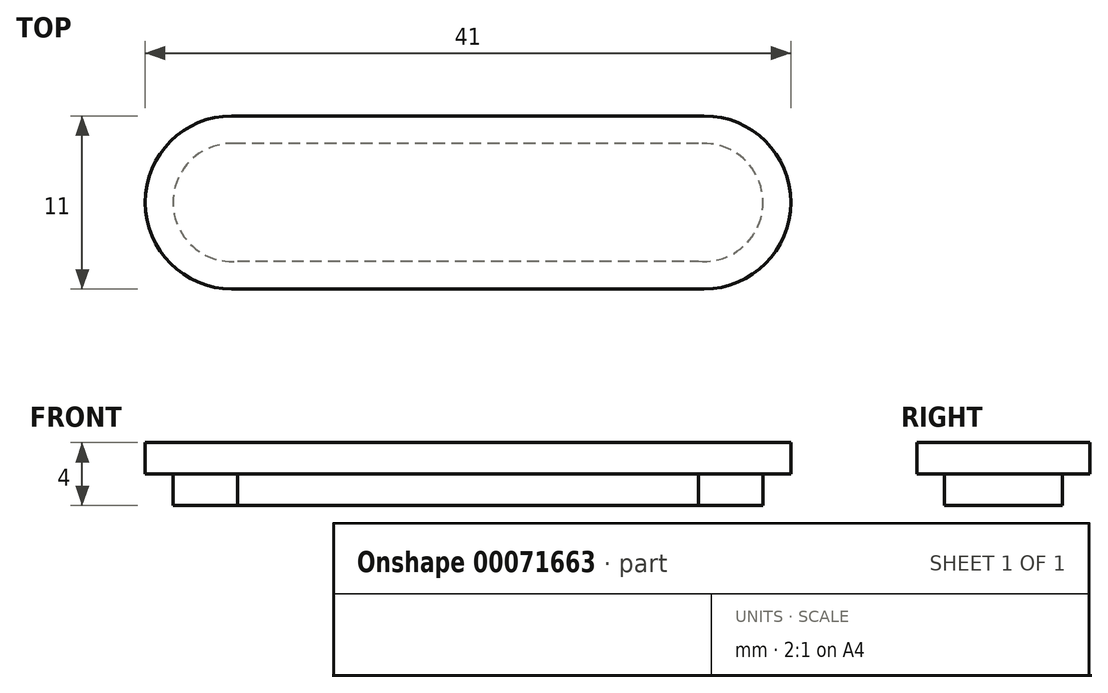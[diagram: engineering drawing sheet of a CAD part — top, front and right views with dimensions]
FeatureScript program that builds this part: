
annotation { "Feature Type Name" : "Feature", "Feature Type Description" : "" }
export const myFeature = defineFeature(function(context is Context, id is Id, definition is map)
    precondition{}
    {
        {
            var Q0;
            Q0=qCreatedBy(makeId("Top.planeOp"),FACE);
            var sketch = newSketch(context, id + "F0", { "sketchPlane" : qUnion([Q0])});
            skLineSegment(sketch, "E0.7", {"start": v(14.14, 5.47) * mm, "end": v(-15.86, 5.47) * mm});
            skLineSegment(sketch, "E0.6", {"start": v(14.14, 3.97) * mm, "end": v(-15.86, 3.97) * mm, "construction": true});
            skArc(sketch, "E0.11", {"start": v(18.14, 0.02) * mm, "mid": v(16.99, -2.84) * mm, "end": v(14.14, -4.03) * mm, "construction": true});
            skArc(sketch, "E0.8", {"start": v(14.14, 3.97) * mm, "mid": v(16.95, 2.82) * mm, "end": v(18.14, 0.02) * mm, "construction": true});
            skArc(sketch, "E0.10", {"start": v(14.14, -5.53) * mm, "mid": v(18.05, -3.9) * mm, "end": v(19.64, 0.03) * mm});
            skArc(sketch, "E0.9", {"start": v(19.64, 0.03) * mm, "mid": v(18, 3.88) * mm, "end": v(14.14, 5.47) * mm});
            skArc(sketch, "E0.0", {"start": v(-15.86, 5.47) * mm, "mid": v(-19.75, 3.86) * mm, "end": v(-21.36, -0.03) * mm});
            skArc(sketch, "E0.1", {"start": v(-21.36, -0.03) * mm, "mid": v(-19.75, -3.92) * mm, "end": v(-15.86, -5.53) * mm});
            skLineSegment(sketch, "E0.2", {"start": v(-15.86, -5.53) * mm, "end": v(14.14, -5.53) * mm});
            skLineSegment(sketch, "E0.3", {"start": v(-15.86, -4.03) * mm, "end": v(14.14, -4.03) * mm, "construction": true});
            skArc(sketch, "E0.4", {"start": v(-15.86, -4.03) * mm, "mid": v(-18.69, -2.85) * mm, "end": v(-19.86, -0.03) * mm, "construction": true});
            skArc(sketch, "E0.5", {"start": v(-19.86, -0.03) * mm, "mid": v(-18.69, 2.8) * mm, "end": v(-15.86, 3.97) * mm, "construction": true});
            skSolve(sketch);
        }
        {
            var Q0;
            Q0=makeQuery(id+"F0.imprint","IMPRINT",FACE,{"disambiguationData":[TD([[makeQuery(id+"F0.imprint","IMPRINT",EDGE,{"derivedFrom":sQuery(id+"F0.wireOp",EDGE,"E0.7")}),1.0]])]});
            var Q1;
            Q1=sQuery(id+"F0.wireOp",EDGE,"E0.7");
            var Q2;
            Q2=sQuery(id+"F0.wireOp",EDGE,"E0.0");
            var Q3;
            Q3=sQuery(id+"F0.wireOp",EDGE,"E0.1");
            var Q4;
            Q4=sQuery(id+"F0.wireOp",EDGE,"E0.2");
            var Q5;
            Q5=sQuery(id+"F0.wireOp",EDGE,"E0.10");
            var Q6;
            Q6=sQuery(id+"F0.wireOp",EDGE,"E0.9");
            extrude(context, id + "F1", {"entities" : qUnion([Q0]), "surfaceEntities" : qUnion([Q1, Q2, Q3, Q4, Q5, Q6]), "depth" : 2 * mm});
        }
        {
            var Q0;
            Q0=makeQuery(id+"F1.opExtrude","CAP_FACE",FACE,{"disambiguationData":[OSD([sQuery(id+"F0.wireOp",EDGE,"E0.7"),sQuery(id+"F0.wireOp",EDGE,"E0.10"),sQuery(id+"F0.wireOp",EDGE,"E0.9"),sQuery(id+"F0.wireOp",EDGE,"E0.0"),sQuery(id+"F0.wireOp",EDGE,"E0.1"),sQuery(id+"F0.wireOp",EDGE,"E0.2")])],"isStart":true});
            var sketch = newSketch(context, id + "F2", { "sketchPlane" : qUnion([Q0])});
            skArc(sketch, "E1.0", {"start": v(-15.86, -5.47) * mm, "mid": v(-21.36, 0.03) * mm, "end": v(-15.86, 5.53) * mm, "construction": true});
            skLineSegment(sketch, "E1.1", {"start": v(-15.86, 5.53) * mm, "end": v(14.14, 5.53) * mm, "construction": true});
            skArc(sketch, "E1.2", {"start": v(14.14, 5.53) * mm, "mid": v(19.64, 0.03) * mm, "end": v(14.14, -5.47) * mm, "construction": true});
            skLineSegment(sketch, "E1.3", {"start": v(14.14, -5.47) * mm, "end": v(-15.86, -5.47) * mm, "construction": true});
            skLineSegment(sketch, "E2.0", {"start": v(-15.5, 3.76) * mm, "end": v(13.78, 3.76) * mm});
            skArc(sketch, "E2.1", {"start": v(-15.5, -3.7) * mm, "mid": v(-19.6, 0.03) * mm, "end": v(-15.5, 3.76) * mm});
            skLineSegment(sketch, "E2.2", {"start": v(13.78, -3.7) * mm, "end": v(-15.5, -3.7) * mm});
            skArc(sketch, "E2.3", {"start": v(13.78, 3.76) * mm, "mid": v(17.87, 0.03) * mm, "end": v(13.78, -3.7) * mm});
            skPoint(sketch, "E3", {"position": v(-19.6, 0.03) * mm});
            skPoint(sketch, "E4", {"position": v(-21.36, 0.03) * mm});
            skPoint(sketch, "E5", {"position": v(19.64, 0.03) * mm});
            skPoint(sketch, "E6", {"position": v(17.87, 0.03) * mm});
            skPoint(sketch, "E7", {"position": v(-0.86, 5.53) * mm});
            skPoint(sketch, "E8", {"position": v(-0.86, 3.76) * mm});
            skPoint(sketch, "E9", {"position": v(-0.86, -3.7) * mm});
            skPoint(sketch, "E10", {"position": v(-0.86, -5.47) * mm});
            skSolve(sketch);
        }
        {
            var Q0;
            Q0=makeQuery(id+"F2.imprint","IMPRINT",FACE,{"disambiguationData":[TD([[makeQuery(id+"F2.imprint","IMPRINT",EDGE,{"derivedFrom":sQuery(id+"F2.wireOp",EDGE,"E2.0")}),-1.0]])]});
            extrude(context, id + "F3", {"entities" : qUnion([Q0]), "operationType" : NewBodyOperationType.ADD, "depth" : 2 * mm});
        }
    });
